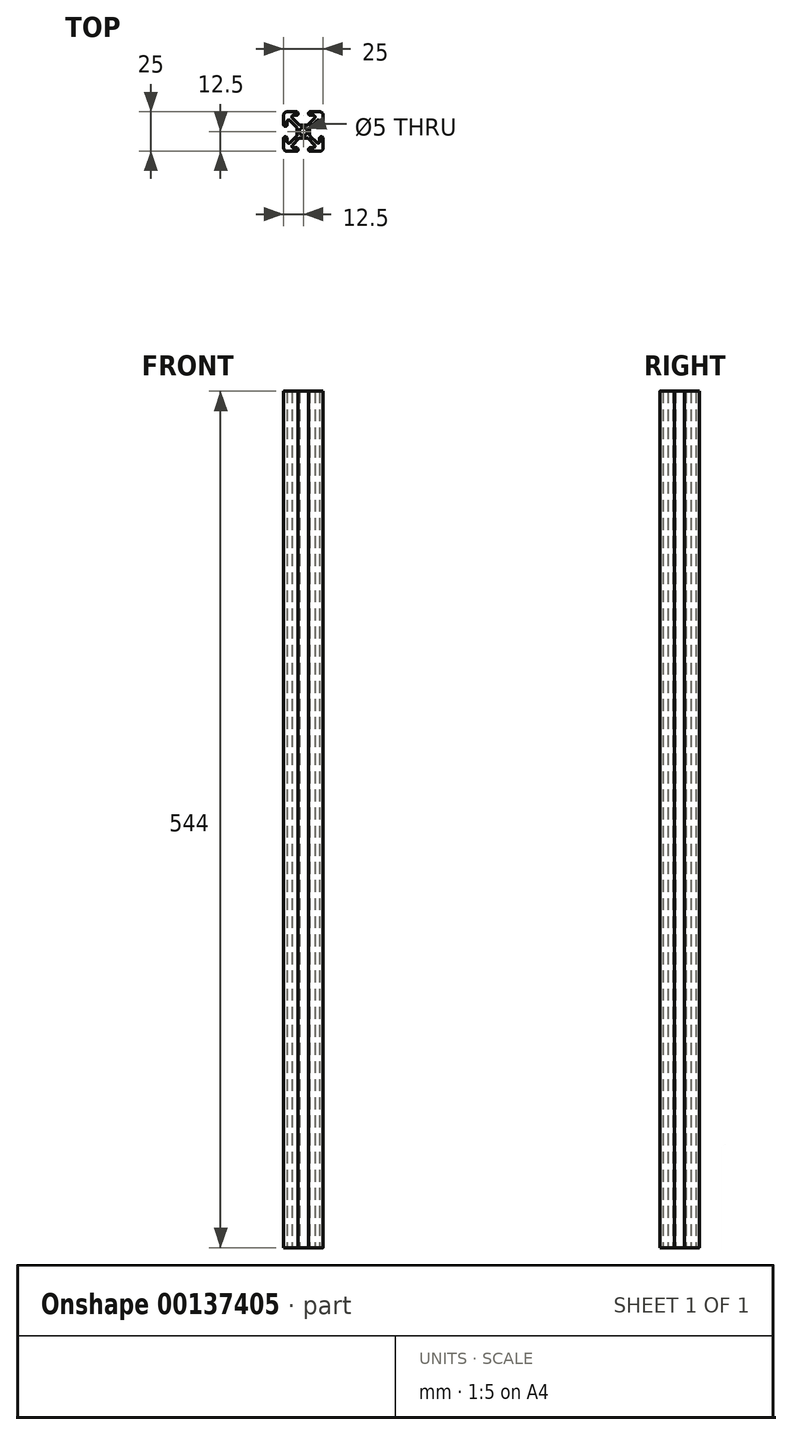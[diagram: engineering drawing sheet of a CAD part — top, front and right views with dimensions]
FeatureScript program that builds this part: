
annotation { "Feature Type Name" : "Feature", "Feature Type Description" : "" }
export const myFeature = defineFeature(function(context is Context, id is Id, definition is map)
    precondition{}
    {
        {
            var Q0;
            Q0=qCreatedBy(makeId("Top.planeOp"),FACE);
            var sketch = newSketch(context, id + "F0", { "sketchPlane" : qUnion([Q0])});
            skCircle(sketch, "E0", {"center": v(0, 0) * mm, "radius": 2.5 * mm});
            skLineSegment(sketch, "E1", {"start": v(0, 0) * mm, "end": v(0, 4.05) * mm, "construction": true});
            skLineSegment(sketch, "E2", {"start": v(0, 0) * mm, "end": v(-4.05, 0) * mm, "construction": true});
            skLineSegment(sketch, "E3", {"start": v(0, 0) * mm, "end": v(-12.5, 12.5) * mm, "construction": true});
            skLineSegment(sketch, "E4", {"start": v(-12.5, 10.36) * mm, "end": v(-12.5, 4.32) * mm});
            skLineSegment(sketch, "E5", {"start": v(-10.36, 12.5) * mm, "end": v(-4.32, 12.5) * mm});
            skLineSegment(sketch, "E6", {"start": v(-4.32, 10.36) * mm, "end": v(-6.26, 10.36) * mm});
            skLineSegment(sketch, "E7", {"start": v(-10.36, 6.26) * mm, "end": v(-10.36, 4.32) * mm});
            skArc(sketch, "E8", {"start": v(-4.32, 12.5) * mm, "mid": v(-3.25, 11.43) * mm, "end": v(-4.32, 10.36) * mm});
            skArc(sketch, "E9", {"start": v(-10.36, 4.32) * mm, "mid": v(-11.43, 3.25) * mm, "end": v(-12.5, 4.32) * mm});
            skLineSegment(sketch, "E10", {"start": v(0, 4.05) * mm, "end": v(-2.1, 4.05) * mm});
            skLineSegment(sketch, "E11", {"start": v(-4.05, 2.1) * mm, "end": v(-4.05, 0) * mm});
            skLineSegment(sketch, "E12", {"start": v(-8.53, 7.02) * mm, "end": v(-4.36, 2.85) * mm});
            skLineSegment(sketch, "E13", {"start": v(-7.02, 8.53) * mm, "end": v(-2.85, 4.36) * mm});
            skLineSegment(sketch, "E14.0.MirrorCS", {"start": v(10.36, 6.26) * mm, "end": v(10.36, 4.32) * mm});
            skLineSegment(sketch, "E14.1.MirrorCS", {"start": v(7.02, 8.53) * mm, "end": v(2.85, 4.36) * mm});
            skArc(sketch, "E14.2.MirrorCS", {"start": v(4.32, 12.5) * mm, "mid": v(3.25, 11.43) * mm, "end": v(4.32, 10.36) * mm});
            skArc(sketch, "E14.3.MirrorCS", {"start": v(10.36, 4.32) * mm, "mid": v(11.43, 3.25) * mm, "end": v(12.5, 4.32) * mm});
            skLineSegment(sketch, "E14.4.MirrorCS", {"start": v(10.36, 12.5) * mm, "end": v(4.32, 12.5) * mm});
            skLineSegment(sketch, "E14.5.MirrorCS", {"start": v(4.32, 10.36) * mm, "end": v(6.26, 10.36) * mm});
            skLineSegment(sketch, "E14.6.MirrorCS", {"start": v(12.5, 10.36) * mm, "end": v(12.5, 4.32) * mm});
            skLineSegment(sketch, "E14.7.MirrorCS", {"start": v(8.53, 7.02) * mm, "end": v(4.36, 2.85) * mm});
            skLineSegment(sketch, "E15.0.MirrorCS", {"start": v(0, 4.05) * mm, "end": v(2.1, 4.05) * mm});
            skLineSegment(sketch, "E16.0.MirrorCS", {"start": v(4.05, 2.1) * mm, "end": v(4.05, 0) * mm});
            skLineSegment(sketch, "E17.0.MirrorCS", {"start": v(10.36, -12.5) * mm, "end": v(4.32, -12.5) * mm});
            skLineSegment(sketch, "E17.1.MirrorCS", {"start": v(12.5, -10.36) * mm, "end": v(12.5, -4.32) * mm});
            skArc(sketch, "E17.2.MirrorCS", {"start": v(4.32, -12.5) * mm, "mid": v(3.25, -11.43) * mm, "end": v(4.32, -10.36) * mm});
            skLineSegment(sketch, "E17.3.MirrorCS", {"start": v(-7.02, -8.53) * mm, "end": v(-2.85, -4.36) * mm});
            skLineSegment(sketch, "E17.4.MirrorCS", {"start": v(7.02, -8.53) * mm, "end": v(2.85, -4.36) * mm});
            skLineSegment(sketch, "E17.5.MirrorCS", {"start": v(10.36, -6.26) * mm, "end": v(10.36, -4.32) * mm});
            skLineSegment(sketch, "E17.6.MirrorCS", {"start": v(8.53, -7.02) * mm, "end": v(4.36, -2.85) * mm});
            skLineSegment(sketch, "E17.7.MirrorCS", {"start": v(-10.36, -12.5) * mm, "end": v(-4.32, -12.5) * mm});
            skLineSegment(sketch, "E17.8.MirrorCS", {"start": v(-4.32, -10.36) * mm, "end": v(-6.26, -10.36) * mm});
            skLineSegment(sketch, "E17.9.MirrorCS", {"start": v(4.32, -10.36) * mm, "end": v(6.26, -10.36) * mm});
            skArc(sketch, "E17.10.MirrorCS", {"start": v(10.36, -4.32) * mm, "mid": v(11.43, -3.25) * mm, "end": v(12.5, -4.32) * mm});
            skLineSegment(sketch, "E17.11.MirrorCS", {"start": v(-12.5, -10.36) * mm, "end": v(-12.5, -4.32) * mm});
            skLineSegment(sketch, "E17.12.MirrorCS", {"start": v(0, -4.05) * mm, "end": v(2.1, -4.05) * mm});
            skArc(sketch, "E17.13.MirrorCS", {"start": v(-4.32, -12.5) * mm, "mid": v(-3.25, -11.43) * mm, "end": v(-4.32, -10.36) * mm});
            skLineSegment(sketch, "E17.14.MirrorCS", {"start": v(-8.53, -7.02) * mm, "end": v(-4.36, -2.85) * mm});
            skArc(sketch, "E17.15.MirrorCS", {"start": v(-10.36, -4.32) * mm, "mid": v(-11.43, -3.25) * mm, "end": v(-12.5, -4.32) * mm});
            skLineSegment(sketch, "E17.16.MirrorCS", {"start": v(-10.36, -6.26) * mm, "end": v(-10.36, -4.32) * mm});
            skLineSegment(sketch, "E17.17.MirrorCS", {"start": v(0, -4.05) * mm, "end": v(-2.1, -4.05) * mm});
            skLineSegment(sketch, "E18.0.MirrorCS", {"start": v(4.05, -2.1) * mm, "end": v(4.05, 0) * mm});
            skLineSegment(sketch, "E19.0.MirrorCS", {"start": v(-4.05, -2.1) * mm, "end": v(-4.05, 0) * mm});
            skPoint(sketch, "E20.visualSharp", {"position": v(-12.5, 12.5) * mm});
            skArc(sketch, "E20.filletArc", {"start": v(-10.36, 12.5) * mm, "mid": v(-11.87, 11.87) * mm, "end": v(-12.5, 10.36) * mm});
            skPoint(sketch, "E21.visualSharp", {"position": v(12.5, 12.5) * mm});
            skArc(sketch, "E21.filletArc", {"start": v(12.5, 10.36) * mm, "mid": v(11.87, 11.87) * mm, "end": v(10.36, 12.5) * mm});
            skPoint(sketch, "E22.visualSharp", {"position": v(12.5, -12.5) * mm});
            skArc(sketch, "E22.filletArc", {"start": v(10.36, -12.5) * mm, "mid": v(11.87, -11.87) * mm, "end": v(12.5, -10.36) * mm});
            skPoint(sketch, "E23.visualSharp", {"position": v(-12.5, -12.5) * mm});
            skArc(sketch, "E23.filletArc", {"start": v(-12.5, -10.36) * mm, "mid": v(-11.87, -11.87) * mm, "end": v(-10.36, -12.5) * mm});
            skPoint(sketch, "E24.visualSharp", {"position": v(4.05, 4.05) * mm});
            skPoint(sketch, "E25.visualSharp", {"position": v(-10.36, 8.85) * mm});
            skArc(sketch, "E25.filletArc", {"start": v(-8.53, 7.02) * mm, "mid": v(-9.7, 7.25) * mm, "end": v(-10.36, 6.26) * mm});
            skPoint(sketch, "E26.visualSharp", {"position": v(-8.85, 10.36) * mm});
            skArc(sketch, "E26.filletArc", {"start": v(-6.26, 10.36) * mm, "mid": v(-7.25, 9.7) * mm, "end": v(-7.02, 8.53) * mm});
            skPoint(sketch, "E27.visualSharp", {"position": v(8.85, 10.36) * mm});
            skArc(sketch, "E27.filletArc", {"start": v(7.02, 8.53) * mm, "mid": v(7.25, 9.7) * mm, "end": v(6.26, 10.36) * mm});
            skPoint(sketch, "E28.visualSharp", {"position": v(10.36, 8.85) * mm});
            skArc(sketch, "E28.filletArc", {"start": v(10.36, 6.26) * mm, "mid": v(9.7, 7.25) * mm, "end": v(8.53, 7.02) * mm});
            skPoint(sketch, "E29.visualSharp", {"position": v(10.36, -8.85) * mm});
            skArc(sketch, "E29.filletArc", {"start": v(8.53, -7.02) * mm, "mid": v(9.7, -7.25) * mm, "end": v(10.36, -6.26) * mm});
            skPoint(sketch, "E30.visualSharp", {"position": v(8.85, -10.36) * mm});
            skArc(sketch, "E30.filletArc", {"start": v(6.26, -10.36) * mm, "mid": v(7.25, -9.7) * mm, "end": v(7.02, -8.53) * mm});
            skPoint(sketch, "E31.visualSharp", {"position": v(-8.85, -10.36) * mm});
            skArc(sketch, "E31.filletArc", {"start": v(-7.02, -8.53) * mm, "mid": v(-7.25, -9.7) * mm, "end": v(-6.26, -10.36) * mm});
            skPoint(sketch, "E32.visualSharp", {"position": v(-10.36, -8.85) * mm});
            skArc(sketch, "E32.filletArc", {"start": v(-10.36, -6.26) * mm, "mid": v(-9.7, -7.25) * mm, "end": v(-8.53, -7.02) * mm});
            skPoint(sketch, "E33.orphan", {"position": v(-4.05, 4.05) * mm});
            skPoint(sketch, "E34.orphan", {"position": v(4.05, -4.05) * mm});
            skPoint(sketch, "E35.orphan", {"position": v(-4.05, -4.05) * mm});
            skPoint(sketch, "E36.visualSharp", {"position": v(-2.54, 4.05) * mm});
            skArc(sketch, "E36.filletArc", {"start": v(-2.85, 4.36) * mm, "mid": v(-2.5, 4.13) * mm, "end": v(-2.1, 4.05) * mm});
            skPoint(sketch, "E37.visualSharp", {"position": v(2.54, 4.05) * mm});
            skArc(sketch, "E37.filletArc", {"start": v(2.1, 4.05) * mm, "mid": v(2.5, 4.13) * mm, "end": v(2.85, 4.36) * mm});
            skPoint(sketch, "E38.visualSharp", {"position": v(-4.05, 2.54) * mm});
            skArc(sketch, "E38.filletArc", {"start": v(-4.05, 2.1) * mm, "mid": v(-4.13, 2.5) * mm, "end": v(-4.36, 2.85) * mm});
            skPoint(sketch, "E39.visualSharp", {"position": v(-4.05, -2.54) * mm});
            skArc(sketch, "E39.filletArc", {"start": v(-4.36, -2.85) * mm, "mid": v(-4.13, -2.5) * mm, "end": v(-4.05, -2.1) * mm});
            skPoint(sketch, "E40.visualSharp", {"position": v(-2.54, -4.05) * mm});
            skArc(sketch, "E40.filletArc", {"start": v(-2.1, -4.05) * mm, "mid": v(-2.5, -4.13) * mm, "end": v(-2.85, -4.36) * mm});
            skPoint(sketch, "E41.visualSharp", {"position": v(2.54, -4.05) * mm});
            skArc(sketch, "E41.filletArc", {"start": v(2.85, -4.36) * mm, "mid": v(2.5, -4.13) * mm, "end": v(2.1, -4.05) * mm});
            skPoint(sketch, "E42.visualSharp", {"position": v(4.05, -2.54) * mm});
            skArc(sketch, "E42.filletArc", {"start": v(4.05, -2.1) * mm, "mid": v(4.13, -2.5) * mm, "end": v(4.36, -2.85) * mm});
            skPoint(sketch, "E43.visualSharp", {"position": v(4.05, 2.54) * mm});
            skArc(sketch, "E43.filletArc", {"start": v(4.36, 2.85) * mm, "mid": v(4.13, 2.5) * mm, "end": v(4.05, 2.1) * mm});
            skSolve(sketch);
        }
        {
            var Q0;
            Q0=qSketchRegion(id+"F0",true);
            extrude(context, id + "F1", {"entities" : qUnion([Q0]), "depth" : 544 * mm});
        }
    });
